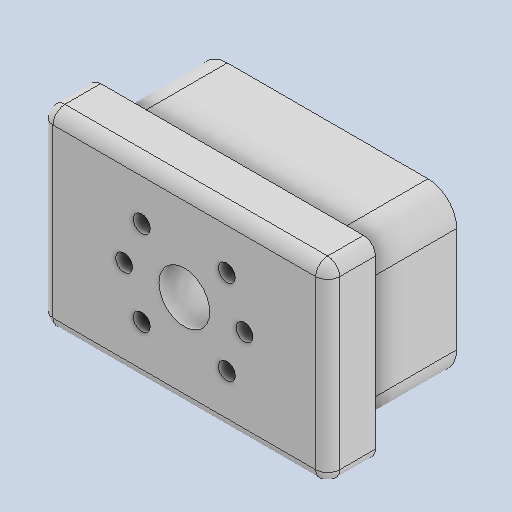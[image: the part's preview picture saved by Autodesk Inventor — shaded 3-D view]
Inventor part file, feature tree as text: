
AUTODESK INVENTOR PART (.ipt)
format: ipt  version: 2023 (Build 270158000, 158)  size: 227,840 bytes
history: native  units: in
note: dims shown in document units (in); Inventor stores cm internally (conversion verified against a paired STEP export)
features: extrude x3, sketch x3, projected_geometry x2, fillet x1, chamfer x1
ambient origin geometry x8: Origin, YZ Plane, XZ Plane, XY Plane, X Axis, Y Axis, Z Axis, Center Point
bodies: Solid1 (feature_tree)
feature tree (10):
  extrude  "Extrusion1"  Depth=1.7in
  extrude  "Extrusion2"  Depth=1.0in TaperAngle=0.0deg
  fillet  "Fillet1"  Radius=3.0in
  extrude  "Extrusion3"  Depth=0.125in
  chamfer  "Chamfer1"  Distance=0.5in
  sketch  "Sketch1"  dims[d0=2.7in d1=1.7in]
  sketch  "Sketch2"  dims[d2=0.3in d3=1.0in d4=0.0in d5=3.0in]
  sketch  "Sketch3"  dims[d6=2.0in d7=0.125in d8=0.5in d9=0.0in d10=0.125in d11=0.5315in d12=0.5in d13=0.0in d14=0.1772in d15=1.2598in d16=45.0deg d17=0.05in d18=0.125in d19=45.0deg]
  projected_geometry  "Projected Loop1"
  projected_geometry  "Projected Loop2"
